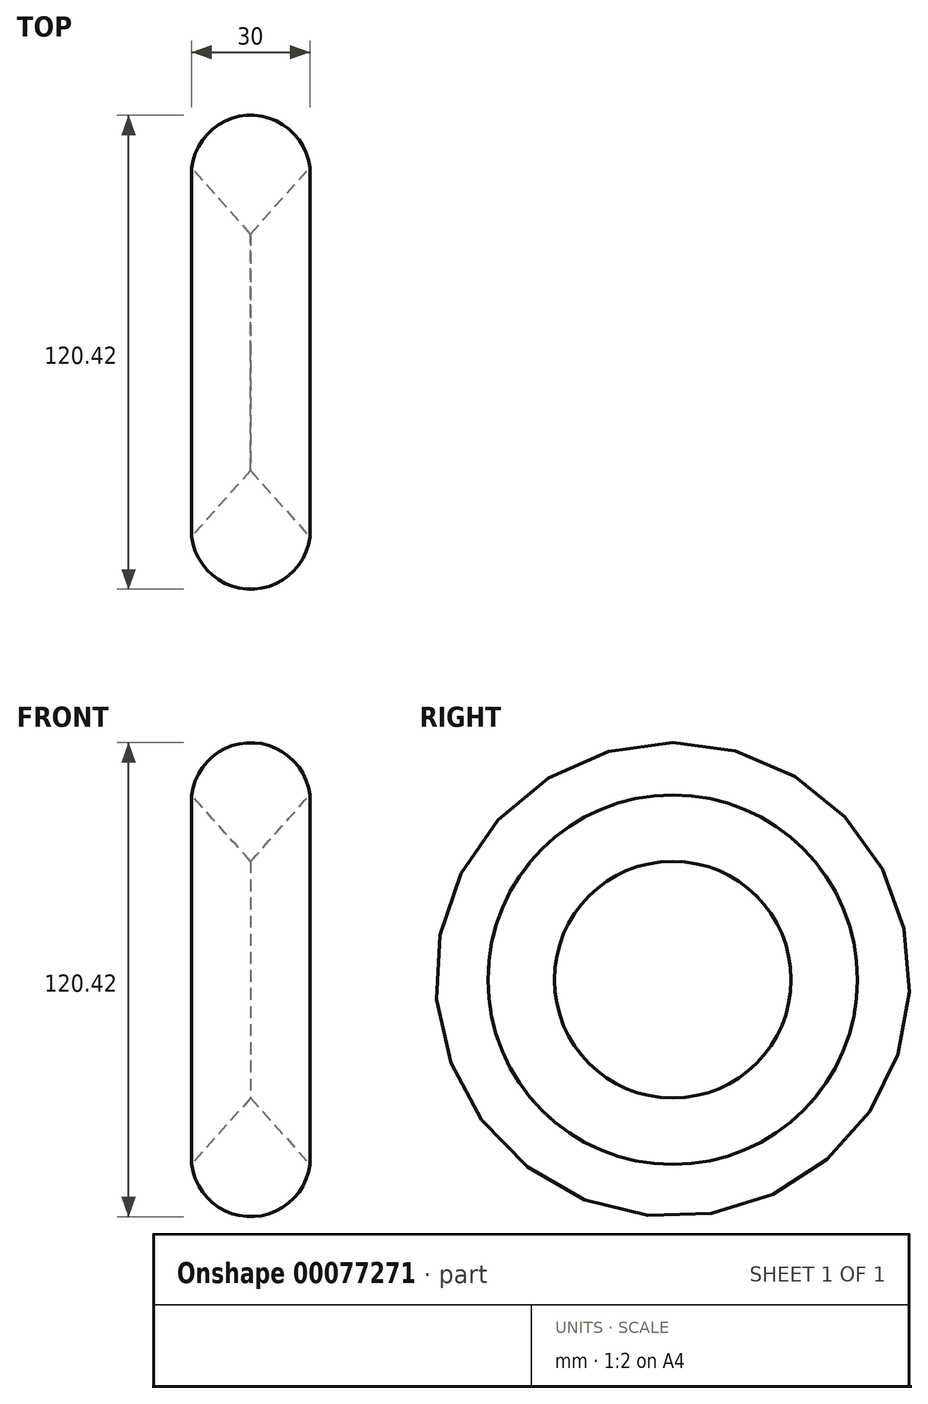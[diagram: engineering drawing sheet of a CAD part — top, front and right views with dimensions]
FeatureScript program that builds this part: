
annotation { "Feature Type Name" : "Feature", "Feature Type Description" : "" }
export const myFeature = defineFeature(function(context is Context, id is Id, definition is map)
    precondition{}
    {
        {
            var Q0;
            Q0=qCreatedBy(makeId("Front.planeOp"),FACE);
            var sketch = newSketch(context, id + "F0", { "sketchPlane" : qUnion([Q0])});
            skLineSegment(sketch, "E0", {"start": v(-80.07, 0) * mm, "end": v(80.07, 0) * mm});
            skLineSegment(sketch, "E1", {"start": v(-15, 0) * mm, "end": v(-15, 46.8) * mm});
            skLineSegment(sketch, "E2", {"start": v(15, 0.16) * mm, "end": v(15, 46.95) * mm});
            skLineSegment(sketch, "E3", {"start": v(-15, 46.8) * mm, "end": v(0, 30.05) * mm});
            skLineSegment(sketch, "E4", {"start": v(0, 30.05) * mm, "end": v(15, 46.95) * mm});
            skArc(sketch, "E5", {"start": v(15, 46.95) * mm, "mid": v(-0.07, 60.21) * mm, "end": v(-15, 46.8) * mm});
            skSolve(sketch);
        }
        {
            var Q0;
            Q0=sQuery(id+"F0.wireOp",EDGE,"E1");
            var Q1;
            Q1=sQuery(id+"F0.wireOp",EDGE,"E3");
            var Q2;
            Q2=sQuery(id+"F0.wireOp",EDGE,"E4");
            var Q3;
            Q3=sQuery(id+"F0.wireOp",EDGE,"E2");
            var Q4;
            Q4=sQuery(id+"F0.wireOp",EDGE,"E0");
            revolve(context, id + "F1", {"bodyType" : ToolBodyType.SURFACE, "surfaceEntities" : qUnion([Q0, Q1, Q2, Q3]), "axis" : qUnion([Q4]), "revolveType" : RevolveType.FULL});
        }
        {
            var Q0;
            Q0=makeQuery(id+"F0.imprint","IMPRINT",FACE,{"disambiguationData":[TD([[makeQuery(id+"F0.imprint","IMPRINT",EDGE,{"derivedFrom":sQuery(id+"F0.wireOp",EDGE,"E3")}),1.0]])]});
            var Q1;
            Q1=sQuery(id+"F0.wireOp",EDGE,"E0");
            revolve(context, id + "F2", {"entities" : qUnion([Q0]), "axis" : qUnion([Q1]), "revolveType" : RevolveType.FULL});
        }
    });
